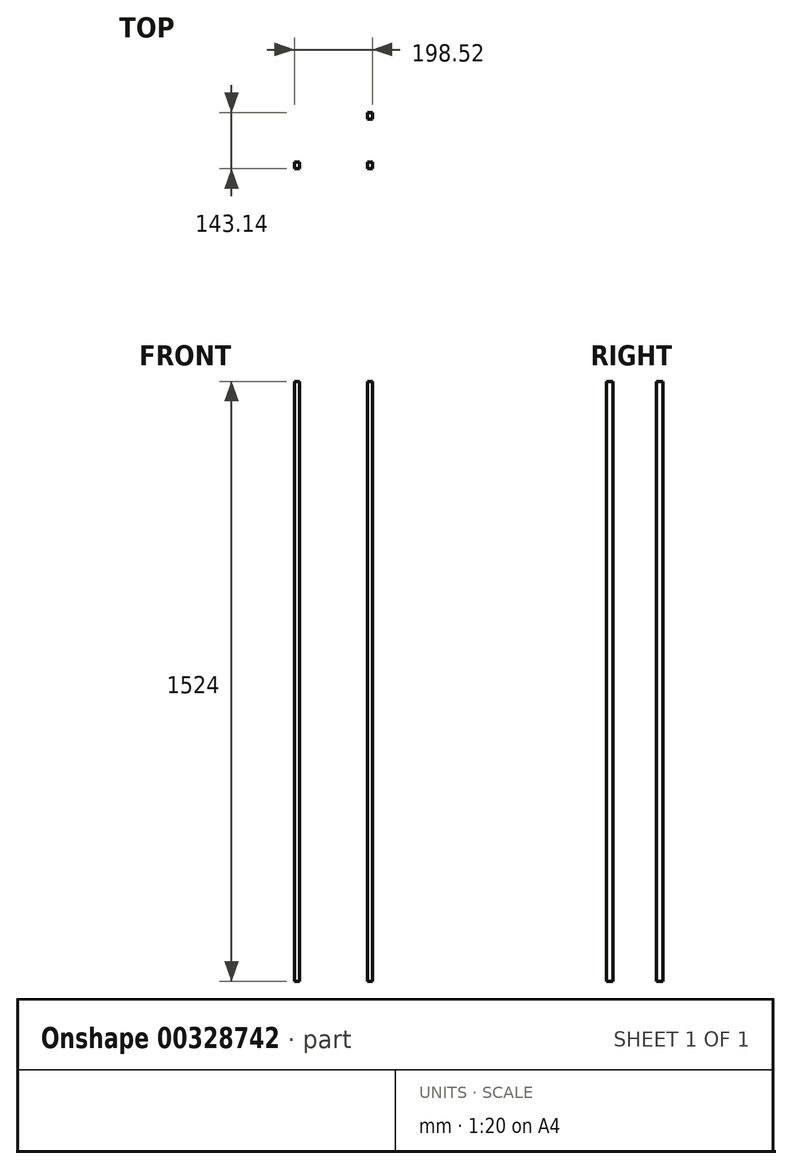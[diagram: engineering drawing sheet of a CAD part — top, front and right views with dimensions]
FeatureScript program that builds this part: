
annotation { "Feature Type Name" : "Feature", "Feature Type Description" : "" }
export const myFeature = defineFeature(function(context is Context, id is Id, definition is map)
    precondition{}
    {
        {
            var Q0;
            Q0=qCreatedBy(makeId("Top.planeOp"),FACE);
            var sketch = newSketch(context, id + "F0", { "sketchPlane" : qUnion([Q0])});
            skLineSegment(sketch, "E0.bottom", {"start": v(99.26, 71.57) * mm, "end": v(-99.26, 71.57) * mm});
            skLineSegment(sketch, "E0.top", {"start": v(99.26, -71.57) * mm, "end": v(-99.26, -71.57) * mm});
            skLineSegment(sketch, "E0.left", {"start": v(99.26, 71.57) * mm, "end": v(99.26, -71.57) * mm});
            skLineSegment(sketch, "E0.right", {"start": v(-99.26, 71.57) * mm, "end": v(-99.26, -71.57) * mm});
            skPoint(sketch, "E0.middle", {"position": v(0, 0) * mm});
            skLineSegment(sketch, "E1.bottom", {"start": v(-99.26, 71.57) * mm, "end": v(-86.1, 71.57) * mm});
            skLineSegment(sketch, "E1.top", {"start": v(-99.26, 55.11) * mm, "end": v(-86.1, 55.11) * mm});
            skLineSegment(sketch, "E1.left", {"start": v(-99.26, 71.57) * mm, "end": v(-99.26, 55.11) * mm});
            skLineSegment(sketch, "E1.right", {"start": v(-86.1, 71.57) * mm, "end": v(-86.1, 55.11) * mm});
            skLineSegment(sketch, "E2.MirrorCS", {"start": v(86.1, 71.57) * mm, "end": v(86.1, 55.11) * mm});
            skLineSegment(sketch, "E3.MirrorCS", {"start": v(99.26, 55.11) * mm, "end": v(86.1, 55.11) * mm});
            skLineSegment(sketch, "E4.MirrorCS", {"start": v(-99.26, -55.11) * mm, "end": v(-86.1, -55.11) * mm});
            skLineSegment(sketch, "E5.MirrorCS", {"start": v(-86.1, -71.57) * mm, "end": v(-86.1, -55.11) * mm});
            skLineSegment(sketch, "E6.MirrorCS", {"start": v(86.1, -71.57) * mm, "end": v(86.1, -55.11) * mm});
            skLineSegment(sketch, "E7.MirrorCS", {"start": v(99.26, -55.11) * mm, "end": v(86.1, -55.11) * mm});
            skSolve(sketch);
        }
        {
            var Q0;
            Q0=makeQuery(id+"F0.imprint","IMPRINT",FACE,{"disambiguationData":[TD([[makeQuery(id+"F0.imprint","IMPRINT",EDGE,{"derivedFrom":sQuery(id+"F0.wireOp",EDGE,"E1.bottom")}),-1.0]])]});
            var Q1;
            {var subQ4=sQuery(id+"F0.wireOp",EDGE,"E4.MirrorCS");Q1=makeQuery(id+"F0.imprint","IMPRINT",FACE,{"disambiguationData":[TD([[makeQuery(id+"F0.imprint","IMPRINT",EDGE,{"derivedFrom":subQ4}),-1.0]])]});}
            var Q2;
            {var subQ3=sQuery(id+"F0.wireOp",EDGE,"E2.MirrorCS");Q2=makeQuery(id+"F0.imprint","IMPRINT",FACE,{"disambiguationData":[TD([[makeQuery(id+"F0.imprint","IMPRINT",EDGE,{"derivedFrom":subQ3}),1.0]])]});}
            var Q3;
            {var subQ3=sQuery(id+"F0.wireOp",EDGE,"E6.MirrorCS");Q3=makeQuery(id+"F0.imprint","IMPRINT",FACE,{"disambiguationData":[TD([[makeQuery(id+"F0.imprint","IMPRINT",EDGE,{"derivedFrom":subQ3}),-1.0]])]});}
            extrude(context, id + "F1", {"entities" : qUnion([Q0, Q1, Q2, Q3]), "depth" : 1524 * mm});
        }
    });
